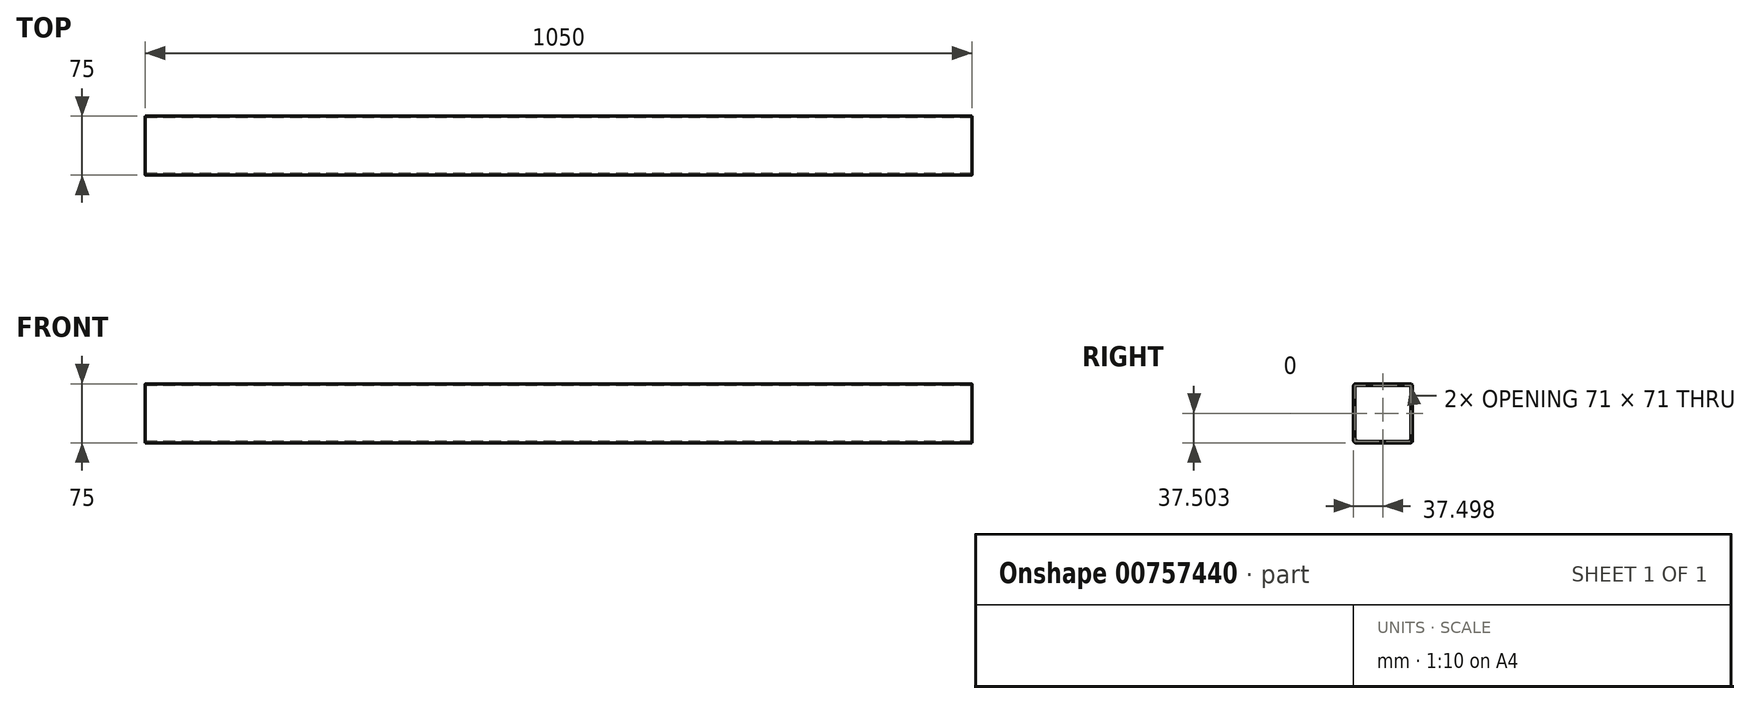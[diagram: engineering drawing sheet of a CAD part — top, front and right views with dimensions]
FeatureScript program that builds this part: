
annotation { "Feature Type Name" : "Feature", "Feature Type Description" : "" }
export const myFeature = defineFeature(function(context is Context, id is Id, definition is map)
    precondition{}
    {
        {
            var Q0;
            Q0=qCreatedBy(makeId("Right.planeOp"),FACE);
            var sketch = newSketch(context, id + "F0", { "sketchPlane" : qUnion([Q0])});
            skLineSegment(sketch, "E0.bottom", {"start": v(-9.8, 57.85) * mm, "end": v(59.2, 57.85) * mm});
            skLineSegment(sketch, "E0.top", {"start": v(-9.8, -17.15) * mm, "end": v(59.2, -17.15) * mm});
            skLineSegment(sketch, "E0.left", {"start": v(-12.8, 54.85) * mm, "end": v(-12.8, -14.15) * mm});
            skLineSegment(sketch, "E0.right", {"start": v(62.2, 54.85) * mm, "end": v(62.2, -14.15) * mm});
            skPoint(sketch, "E1.visualSharp", {"position": v(-12.8, 57.85) * mm});
            skArc(sketch, "E1.filletArc", {"start": v(-9.8, 57.85) * mm, "mid": v(-11.91, 56.97) * mm, "end": v(-12.8, 54.85) * mm});
            skPoint(sketch, "E2.visualSharp", {"position": v(62.2, 57.85) * mm});
            skArc(sketch, "E2.filletArc", {"start": v(62.2, 54.85) * mm, "mid": v(61.33, 56.97) * mm, "end": v(59.2, 57.85) * mm});
            skPoint(sketch, "E3.visualSharp", {"position": v(62.2, -17.15) * mm});
            skArc(sketch, "E3.filletArc", {"start": v(59.2, -17.15) * mm, "mid": v(61.33, -16.27) * mm, "end": v(62.2, -14.15) * mm});
            skPoint(sketch, "E4.visualSharp", {"position": v(-12.8, -17.15) * mm});
            skArc(sketch, "E4.filletArc", {"start": v(-12.8, -14.15) * mm, "mid": v(-11.91, -16.27) * mm, "end": v(-9.8, -17.15) * mm});
            skLineSegment(sketch, "E5.0", {"start": v(60.2, 52.85) * mm, "end": v(60.2, -12.15) * mm});
            skLineSegment(sketch, "E5.1", {"start": v(-7.8, 55.85) * mm, "end": v(57.2, 55.85) * mm});
            skLineSegment(sketch, "E5.2", {"start": v(-10.8, 52.85) * mm, "end": v(-10.8, -12.15) * mm});
            skLineSegment(sketch, "E5.3", {"start": v(-7.8, -15.15) * mm, "end": v(57.2, -15.15) * mm});
            skPoint(sketch, "E6.visualSharp", {"position": v(60.2, 55.85) * mm});
            skArc(sketch, "E6.filletArc", {"start": v(60.2, 52.85) * mm, "mid": v(59.33, 54.97) * mm, "end": v(57.2, 55.85) * mm});
            skPoint(sketch, "E7.visualSharp", {"position": v(60.2, -15.15) * mm});
            skArc(sketch, "E7.filletArc", {"start": v(57.2, -15.15) * mm, "mid": v(59.33, -14.27) * mm, "end": v(60.2, -12.15) * mm});
            skPoint(sketch, "E8.visualSharp", {"position": v(-10.8, -15.15) * mm});
            skArc(sketch, "E8.filletArc", {"start": v(-10.8, -12.15) * mm, "mid": v(-9.91, -14.27) * mm, "end": v(-7.8, -15.15) * mm});
            skPoint(sketch, "E9.visualSharp", {"position": v(-10.8, 55.85) * mm});
            skArc(sketch, "E9.filletArc", {"start": v(-7.8, 55.85) * mm, "mid": v(-9.91, 54.97) * mm, "end": v(-10.8, 52.85) * mm});
            skSolve(sketch);
        }
        {
            var Q0;
            Q0 = qSketchRegion(id + "F0", true);
            extrude(context, id + "F1", {"entities" : qUnion([Q0]), "depth" : 1050 * mm, "offsetDistance" : 25 * mm});
        }
    });
